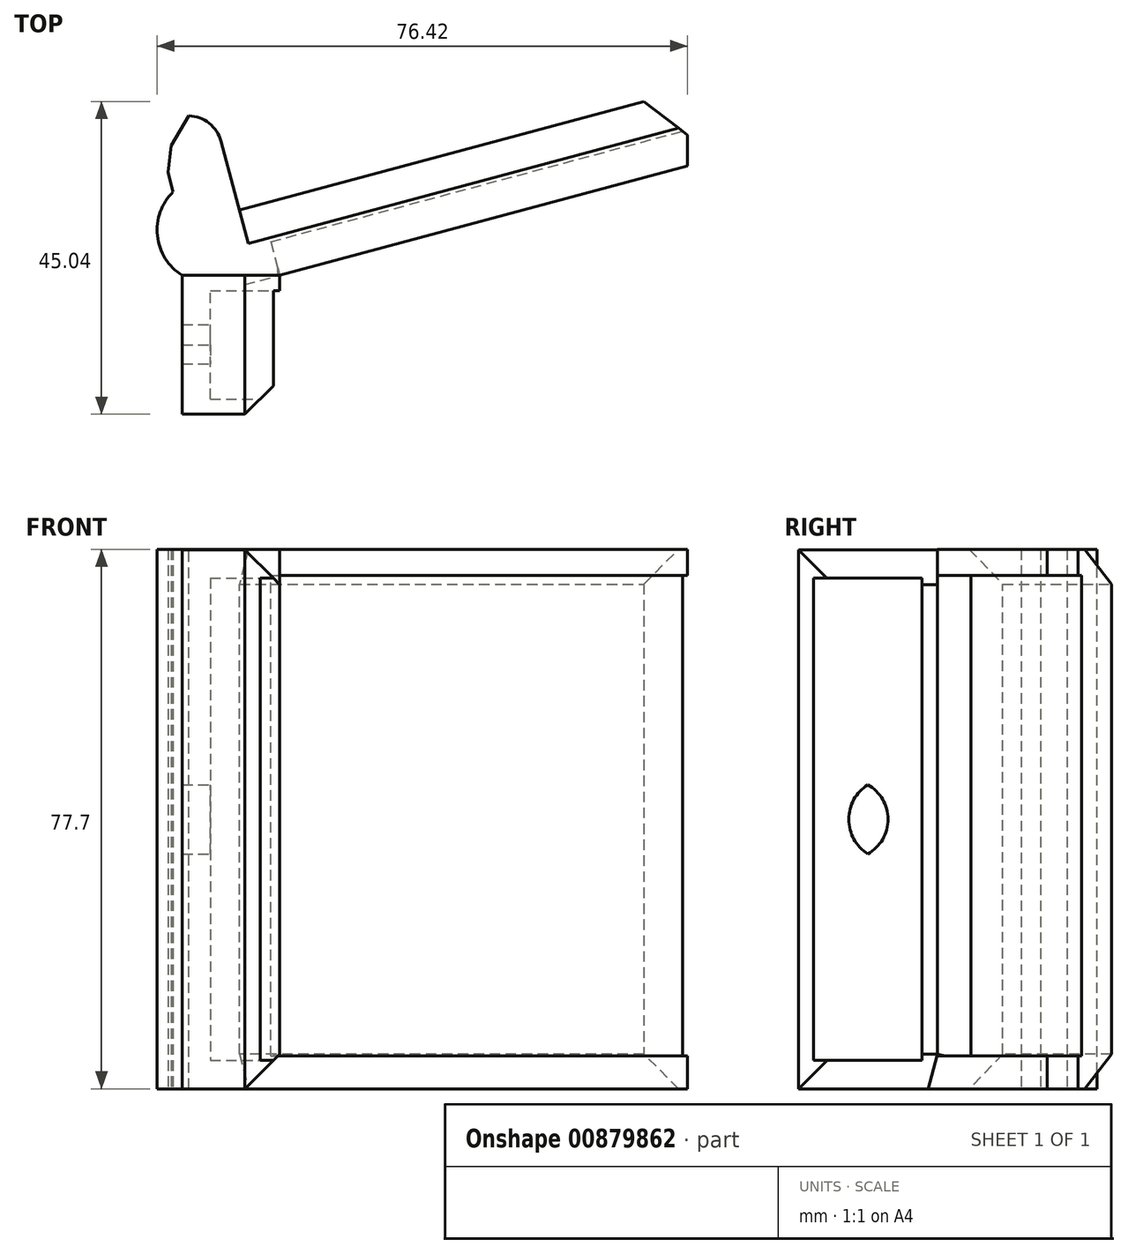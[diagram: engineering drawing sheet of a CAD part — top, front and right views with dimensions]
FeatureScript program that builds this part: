
annotation { "Feature Type Name" : "Feature", "Feature Type Description" : "" }
export const myFeature = defineFeature(function(context is Context, id is Id, definition is map)
    precondition{}
    {
        {
            var Q0;
            Q0=qCreatedBy(makeId("Front.planeOp"),FACE);
            var sketch = newSketch(context, id + "F0", { "sketchPlane" : qUnion([Q0])});
            skLineSegment(sketch, "E0", {"start": v(0, 0) * mm, "end": v(14.05, 0) * mm});
            skLineSegment(sketch, "E1", {"start": v(14.05, 0) * mm, "end": v(14.05, 77.63) * mm});
            skLineSegment(sketch, "E2", {"start": v(14.05, 77.63) * mm, "end": v(0, 77.63) * mm});
            skLineSegment(sketch, "E3", {"start": v(0, 77.63) * mm, "end": v(0, 0) * mm});
            skSolve(sketch);
        }
        {
            var Q0;
            Q0 = qSketchRegion(id + "F0", true);
            extrude(context, id + "F1", {"entities" : qUnion([Q0]), "depth" : 20 * mm, "offsetDistance" : 25 * mm});
        }
        {
            var Q0;
            Q0=makeQuery(id+"F1.opExtrude","SWEPT_FACE",FACE,{"disambiguationData":[OSD([sQuery(id+"F0.wireOp",EDGE,"E0")])]});
            var sketch = newSketch(context, id + "F2", { "sketchPlane" : qUnion([Q0])});
            skLineSegment(sketch, "E4", {"start": v(0, 0) * mm, "end": v(0, -7.2) * mm});
            skLineSegment(sketch, "E5", {"start": v(0, 0) * mm, "end": v(14.05, 0) * mm});
            skLineSegment(sketch, "E6", {"start": v(14.05, 0) * mm, "end": v(72.8, -15.77) * mm});
            skLineSegment(sketch, "E7", {"start": v(0, -7.2) * mm, "end": v(72.8, -26.73) * mm});
            skLineSegment(sketch, "E8", {"start": v(72.8, -26.73) * mm, "end": v(72.8, -15.77) * mm});
            skSolve(sketch);
        }
        {
            var Q0;
            Q0 = qSketchRegion(id + "F2", true);
            extrude(context, id + "F3", {"entities" : qUnion([Q0]), "operationType" : NewBodyOperationType.ADD, "oppositeDirection" : true, "depth" : 77.7 * mm, "offsetDistance" : 25 * mm});
        }
        {
            var Q0;
            Q0=makeQuery(id+"F1.opExtrude","SWEPT_FACE",FACE,{"disambiguationData":[OSD([sQuery(id+"F0.wireOp",EDGE,"E1")])]});
            var sketch = newSketch(context, id + "F4", { "sketchPlane" : qUnion([Q0])});
            skLineSegment(sketch, "E9", {"start": v(-2.24, 38.81) * mm, "end": v(-2.24, 4.08) * mm});
            skLineSegment(sketch, "E10", {"start": v(-2.24, 4.08) * mm, "end": v(-17.83, 4.08) * mm});
            skLineSegment(sketch, "E11", {"start": v(-17.83, 4.08) * mm, "end": v(-17.83, 73.55) * mm});
            skLineSegment(sketch, "E12", {"start": v(-17.83, 73.55) * mm, "end": v(-2.24, 73.55) * mm});
            skLineSegment(sketch, "E13", {"start": v(-2.24, 73.55) * mm, "end": v(-2.24, 38.81) * mm});
            skSolve(sketch);
        }
        {
            var Q0;
            Q0 = qSketchRegion(id + "F4", true);
            extrude(context, id + "F5", {"entities" : qUnion([Q0]), "operationType" : NewBodyOperationType.REMOVE, "oppositeDirection" : true, "depth" : 10 * mm, "offsetDistance" : 25 * mm});
        }
        {
            var Q0;
            Q0=makeQuery(id+"F3.opExtrude","SWEPT_FACE",FACE,{"disambiguationData":[OSD([sQuery(id+"F2.wireOp",EDGE,"E6")])]});
            var sketch = newSketch(context, id + "F6", { "sketchPlane" : qUnion([Q0])});
            skLineSegment(sketch, "E14", {"start": v(13.57, 73.94) * mm, "end": v(74.4, 73.94) * mm});
            skLineSegment(sketch, "E15", {"start": v(13.57, 4.71) * mm, "end": v(74.4, 4.71) * mm});
            skLineSegment(sketch, "E16", {"start": v(13.57, 73.94) * mm, "end": v(13.57, 4.71) * mm});
            skLineSegment(sketch, "E17", {"start": v(74.4, 73.94) * mm, "end": v(80.1, 73.94) * mm});
            skLineSegment(sketch, "E18", {"start": v(80.1, 73.94) * mm, "end": v(80.1, 4.71) * mm});
            skLineSegment(sketch, "E19", {"start": v(80.1, 4.71) * mm, "end": v(74.4, 4.71) * mm});
            skSolve(sketch);
        }
        {
            var Q0;
            Q0 = qSketchRegion(id + "F6", true);
            extrude(context, id + "F7", {"entities" : qUnion([Q0]), "operationType" : NewBodyOperationType.REMOVE, "oppositeDirection" : true, "depth" : 5 * mm, "offsetDistance" : 25 * mm});
        }
        {
            var Q0;
            Q0=makeQuery(id+"F3.opExtrude","SWEPT_FACE",FACE,{"disambiguationData":[OSD([sQuery(id+"F2.wireOp",EDGE,"E7")])]});
            var sketch = newSketch(context, id + "F8", { "sketchPlane" : qUnion([Q0])});
            skLineSegment(sketch, "E20", {"start": v(-1.86, 0) * mm, "end": v(-10.42, 0) * mm});
            skLineSegment(sketch, "E21", {"start": v(-10.42, 0) * mm, "end": v(-10.42, 77.7) * mm});
            skLineSegment(sketch, "E22", {"start": v(-10.42, 77.7) * mm, "end": v(-1.86, 77.7) * mm});
            skLineSegment(sketch, "E23", {"start": v(-1.86, 77.7) * mm, "end": v(-1.86, 0) * mm});
            skSolve(sketch);
        }
        {
            var Q0;
            Q0 = qSketchRegion(id + "F8", true);
            extrude(context, id + "F9", {"entities" : qUnion([Q0]), "operationType" : NewBodyOperationType.ADD, "depth" : 15 * mm, "offsetDistance" : 25 * mm});
        }
        {
            var Q0;
            Q0=makeQuery(id+"F9.opExtrude","CAP_EDGE",EDGE,{"disambiguationData":[OSD([sQuery(id+"F8.wireOp",EDGE,"E23")])],"isStart":false});
            chamfer(context, id + "F10", {"entities" : qUnion([Q0]), "width" : 5 * mm, "tangentPropagation" : true});
        }
        {
            var Q0;
            {var subQ0=sQuery(id+"F8.wireOp",EDGE,"E23");Q0=makeQuery(id+"F10.opChamfer","BLEND_EDGE",EDGE,{"blendedFrom":[makeQuery(id+"F9.opExtrude","CAP_EDGE",EDGE,{"disambiguationData":[OSD([subQ0])],"isStart":false}),makeQuery(id+"F9.opExtrude","SWEPT_FACE",FACE,{"disambiguationData":[OSD([subQ0])]})],"blendedInto":[makeQuery(id+"F9.opExtrude","SWEPT_FACE",FACE,{"disambiguationData":[OSD([subQ0])]})]});}
            chamfer(context, id + "F11", {"entities" : qUnion([Q0]), "width" : 5 * mm, "tangentPropagation" : true});
        }
        {
            var Q0;
            Q0=makeQuery(id+"F9.opExtrude","CAP_EDGE",EDGE,{"disambiguationData":[OSD([sQuery(id+"F8.wireOp",EDGE,"E21")])],"isStart":false});
            fillet(context, id + "F12", {"entities" : qUnion([Q0]), "radius" : 5 * mm, "tangentPropagation" : true, "allowEdgeOverflow" : false});
        }
        {
            var Q0;
            Q0=makeQuery(id+"F3.opExtrude","CAP_EDGE",EDGE,{"disambiguationData":[OSD([sQuery(id+"F2.wireOp",EDGE,"E7")])],"isStart":true});
            var Q1;
            Q1=makeQuery(id+"F3.opExtrude","CAP_EDGE",EDGE,{"disambiguationData":[OSD([sQuery(id+"F2.wireOp",EDGE,"E7")])],"isStart":false});
            var Q2;
            Q2=makeQuery(id+"F3.opExtrude","SWEPT_EDGE",EDGE,{"disambiguationData":[OSD([sQuery(id+"F2.wireOp",EDGE,"E7"),sQuery(id+"F2.wireOp",EDGE,"E8")])]});
            chamfer(context, id + "F13", {"entities" : qUnion([Q0, Q1, Q2]), "width" : 5 * mm, "tangentPropagation" : true});
        }
        {
            var Q0;
            Q0=makeQuery(id+"F1.opExtrude","SWEPT_EDGE",EDGE,{"disambiguationData":[OSD([sQuery(id+"F0.wireOp",EDGE,"E1"),sQuery(id+"F0.wireOp",EDGE,"E2")])]});
            var Q1;
            Q1=makeQuery(id+"F1.opExtrude","CAP_EDGE",EDGE,{"disambiguationData":[OSD([sQuery(id+"F0.wireOp",EDGE,"E1")])],"isStart":false});
            var Q2;
            Q2=makeQuery(id+"F1.opExtrude","SWEPT_EDGE",EDGE,{"disambiguationData":[OSD([sQuery(id+"F0.wireOp",EDGE,"E0"),sQuery(id+"F0.wireOp",EDGE,"E1")])]});
            chamfer(context, id + "F14", {"entities" : qUnion([Q0, Q1, Q2]), "width" : 5 * mm, "tangentPropagation" : true});
        }
        {
            var Q0;
            Q0=makeQuery(id+"F5.boolean.opBoolean","COPY",FACE,{"derivedFrom":makeQuery(id+"F5.opExtrude","CAP_FACE",FACE,{"disambiguationData":[OSD([sQuery(id+"F4.wireOp",EDGE,"E9"),sQuery(id+"F4.wireOp",EDGE,"E10"),sQuery(id+"F4.wireOp",EDGE,"E11"),sQuery(id+"F4.wireOp",EDGE,"E12"),sQuery(id+"F4.wireOp",EDGE,"E13")])],"isStart":false})});
            var sketch = newSketch(context, id + "F15", { "sketchPlane" : qUnion([Q0])});
            skLineSegment(sketch, "E24", {"start": v(-10.04, 73.55) * mm, "end": v(-10.04, 4.08) * mm});
            skArc(sketch, "E25", {"start": v(-10.04, 33.84) * mm, "mid": v(-7.13, 38.82) * mm, "end": v(-10.04, 43.8) * mm});
            skArc(sketch, "E26", {"start": v(-10.04, 43.8) * mm, "mid": v(-12.79, 38.82) * mm, "end": v(-10.04, 33.84) * mm});
            skSolve(sketch);
        }
        {
            var Q0;
            Q0 = qSketchRegion(id + "F15", true);
            extrude(context, id + "F16", {"entities" : qUnion([Q0]), "operationType" : NewBodyOperationType.REMOVE, "oppositeDirection" : true, "depth" : 25 * mm, "offsetDistance" : 25 * mm});
        }
        {
            var Q0;
            Q0=makeQuery(id+"F9.boolean.opBoolean","MERGE",FACE,{"derivedFrom":[makeQuery(id+"F3.boolean.opBoolean","MERGE",FACE,{"derivedFrom":[makeQuery(id+"F1.opExtrude","SWEPT_FACE",FACE,{"disambiguationData":[OSD([sQuery(id+"F0.wireOp",EDGE,"E0")])]}),makeQuery(id+"F3.opExtrude","CAP_FACE",FACE,{"disambiguationData":[OSD([sQuery(id+"F2.wireOp",EDGE,"E4"),sQuery(id+"F2.wireOp",EDGE,"E5"),sQuery(id+"F2.wireOp",EDGE,"E6"),sQuery(id+"F2.wireOp",EDGE,"E7"),sQuery(id+"F2.wireOp",EDGE,"E8")])],"isStart":true})]}),makeQuery(id+"F9.opExtrude","SWEPT_FACE",FACE,{"disambiguationData":[OSD([sQuery(id+"F8.wireOp",EDGE,"E20")])]})]});
            var sketch = newSketch(context, id + "F17", { "sketchPlane" : qUnion([Q0])});
            skArc(sketch, "E27", {"start": v(0, 0) * mm, "mid": v(-3.57, -5.7) * mm, "end": v(-1.3, -12.02) * mm});
            skLineSegment(sketch, "E28", {"start": v(0, 0) * mm, "end": v(0, -7.2) * mm});
            skLineSegment(sketch, "E29", {"start": v(0, -7.2) * mm, "end": v(-1.3, -12.02) * mm});
            skSolve(sketch);
        }
        {
            var Q0;
            Q0 = qSketchRegion(id + "F17", true);
            extrude(context, id + "F18", {"entities" : qUnion([Q0]), "operationType" : NewBodyOperationType.ADD, "oppositeDirection" : true, "depth" : 77.7 * mm, "offsetDistance" : 25 * mm});
        }
    });
